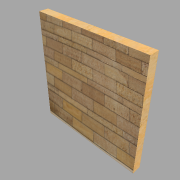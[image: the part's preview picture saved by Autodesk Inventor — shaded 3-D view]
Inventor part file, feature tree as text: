
AUTODESK INVENTOR PART (.ipt)
format: ipt  version: 2022.2 (Build 262287000, 287)  size: 126,464 bytes
history: native  units: in
note: dims shown in document units (in); Inventor stores cm internally (conversion verified against a paired STEP export)
features: extrude x1, sketch x1
ambient origin geometry x8: Origin, YZ Plane, XZ Plane, XY Plane, X Axis, Y Axis, Z Axis, Center Point
bodies: Solid1 (feature_tree)
feature tree (2):
  extrude  "Extrusion1"  Depth=12.0in
  sketch  "Sketch1"  dims[d0=12.0in d1=12.0in d2=1.0in d3=0.0in]
